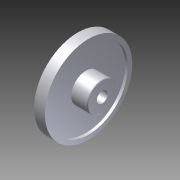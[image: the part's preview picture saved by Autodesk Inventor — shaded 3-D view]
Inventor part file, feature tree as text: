
AUTODESK INVENTOR PART (.ipt)
format: ipt  version: 2012 (Build 160160000, 160)  size: 606,208 bytes
history: native  units: in
note: dims shown in document units (in); Inventor stores cm internally (conversion verified against a paired STEP export)
features: extrude x2, sketch x1, imported_body x1
ambient origin geometry x8: Origin, YZ Plane, XZ Plane, XY Plane, X Axis, Y Axis, Z Axis, Center Point
feature tree (4):
  sketch  "Sketch1"  dims[d0=0.25in d1=0.5625in d2=0.0in d3=2.0in d4=1.0in d5=0.0in]
  extrude  "Extrusion1"  Depth=0.5625in TaperAngle=0.0deg
  extrude  "Extrusion2"  Depth=2.0in
  imported_body  "Base1"
